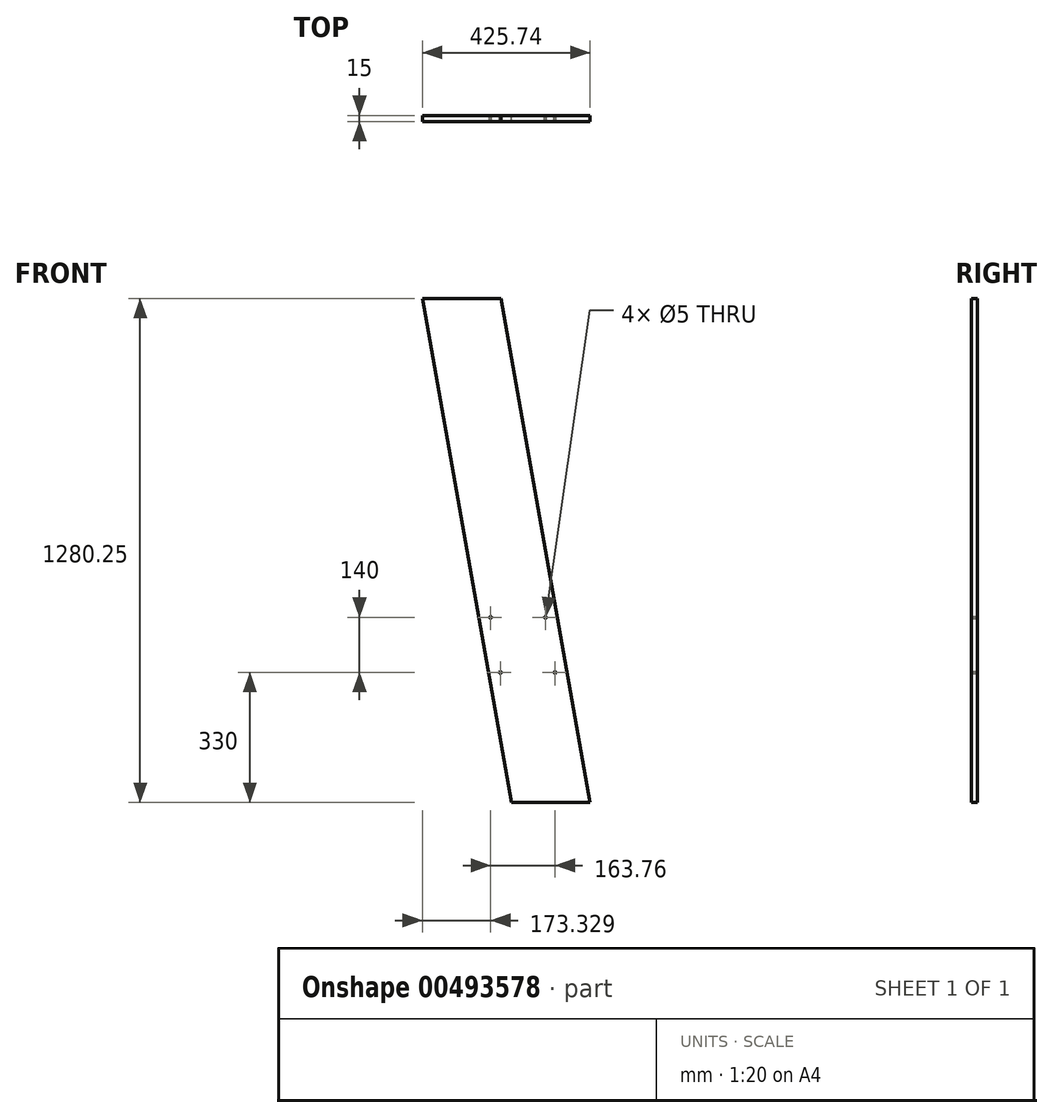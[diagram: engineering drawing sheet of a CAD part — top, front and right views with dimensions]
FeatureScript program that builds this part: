
annotation { "Feature Type Name" : "Feature", "Feature Type Description" : "" }
export const myFeature = defineFeature(function(context is Context, id is Id, definition is map)
    precondition{}
    {
        {
            var Q0;
            Q0=qCreatedBy(makeId("Front.planeOp"),FACE);
            var sketch = newSketch(context, id + "F0", { "sketchPlane" : qUnion([Q0])});
            skLineSegment(sketch, "E0", {"start": v(-225.74, 1280.25) * mm, "end": v(-25.74, 1280.25) * mm});
            skLineSegment(sketch, "E1", {"start": v(-25.74, 1280.25) * mm, "end": v(200, 0) * mm});
            skLineSegment(sketch, "E2", {"start": v(200, 0) * mm, "end": v(0, 0) * mm});
            skLineSegment(sketch, "E3", {"start": v(0, 0) * mm, "end": v(-225.74, 1280.25) * mm});
            skLineSegment(sketch, "E4", {"start": v(-88.16, 500) * mm, "end": v(111.84, 500) * mm});
            skLineSegment(sketch, "E5", {"start": v(-52.9, 300) * mm, "end": v(147.1, 300) * mm});
            skLineSegment(sketch, "E6.0", {"start": v(-55.29, 1275.04) * mm, "end": v(170.46, -5.2) * mm, "construction": true});
            skLineSegment(sketch, "E7.0", {"start": v(29.54, 5.2) * mm, "end": v(-196.2, 1285.46) * mm, "construction": true});
            skLineSegment(sketch, "E8.0", {"start": v(-88.16, 470) * mm, "end": v(111.84, 470) * mm, "construction": true});
            skLineSegment(sketch, "E9.0", {"start": v(-52.9, 330) * mm, "end": v(147.1, 330) * mm, "construction": true});
            skCircle(sketch, "E10", {"center": v(-52.41, 470) * mm, "radius": 2.5 * mm});
            skPoint(sketch, "E10.centerSnap0", {"position": v(11.84, 470) * mm});
            skCircle(sketch, "E11", {"center": v(86.66, 470) * mm, "radius": 2.5 * mm});
            skCircle(sketch, "E12", {"center": v(111.35, 330) * mm, "radius": 2.5 * mm});
            skCircle(sketch, "E13", {"center": v(-27.73, 330) * mm, "radius": 2.5 * mm});
            skSolve(sketch);
        }
        {
            var Q0;
            {var subQ0=sQuery(id+"F0.wireOp",EDGE,"E0");Q0=makeQuery(id+"F0.imprint","IMPRINT",FACE,{"disambiguationData":[TD([[makeQuery(id+"F0.imprint","IMPRINT",EDGE,{"derivedFrom":subQ0}),-1.0]])]});}
            var Q1;
            {var subQ1=sQuery(id+"F0.wireOp",EDGE,"E4");Q1=makeQuery(id+"F0.imprint","IMPRINT",FACE,{"disambiguationData":[TD([[makeQuery(id+"F0.imprint","IMPRINT",EDGE,{"derivedFrom":subQ1}),-1.0]])]});}
            var Q2;
            {var subQ0=sQuery(id+"F0.wireOp",EDGE,"E2");Q2=makeQuery(id+"F0.imprint","IMPRINT",FACE,{"disambiguationData":[TD([[makeQuery(id+"F0.imprint","IMPRINT",EDGE,{"derivedFrom":subQ0}),-1.0]])]});}
            extrude(context, id + "F1", {"entities" : qUnion([Q0, Q1, Q2]), "endBound" : BoundingType.SYMMETRIC, "depth" : 15 * mm});
        }
    });
